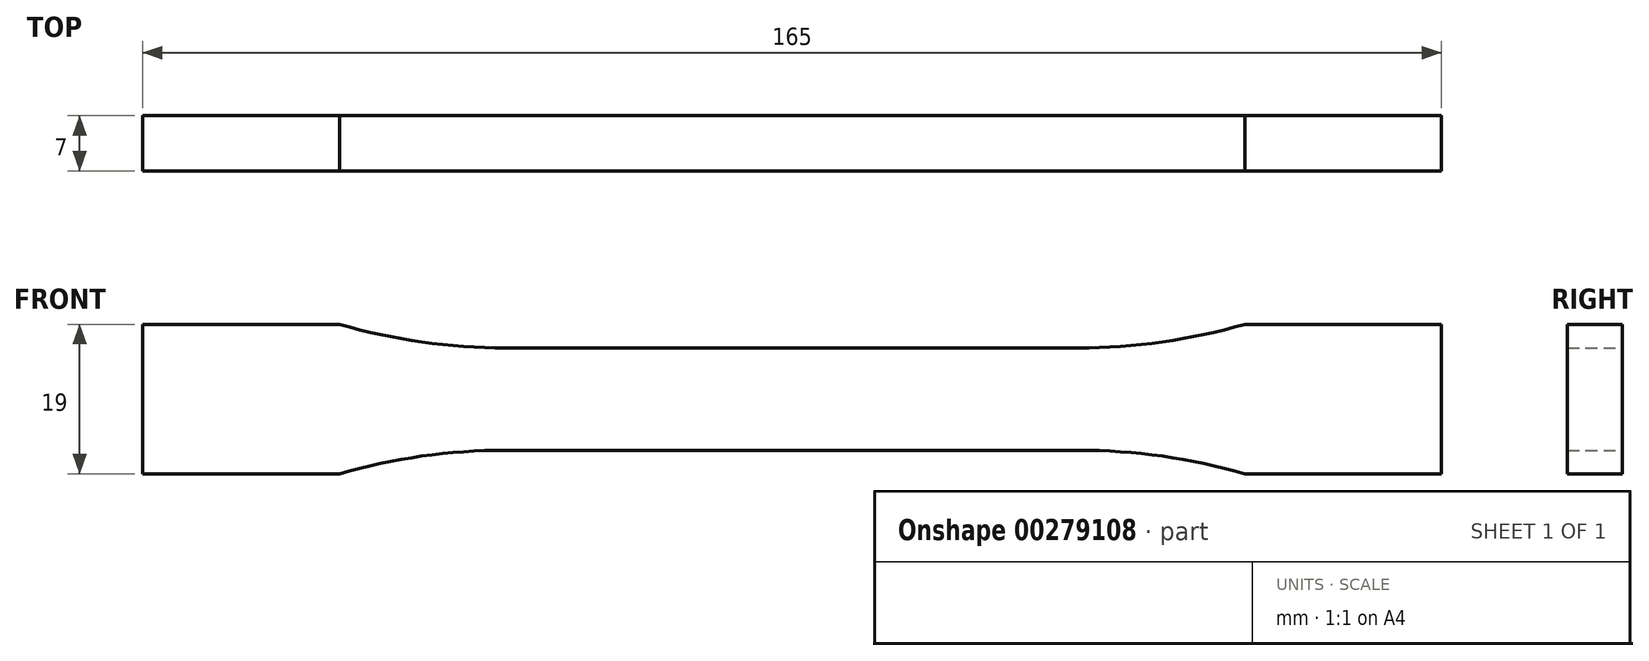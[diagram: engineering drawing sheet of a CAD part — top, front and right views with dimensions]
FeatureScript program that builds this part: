
annotation { "Feature Type Name" : "Feature", "Feature Type Description" : "" }
export const myFeature = defineFeature(function(context is Context, id is Id, definition is map)
    precondition{}
    {
        {
            var Q0;
            Q0=qCreatedBy(makeId("Front.planeOp"),FACE);
            var sketch = newSketch(context, id + "F0", { "sketchPlane" : qUnion([Q0])});
            skLineSegment(sketch, "E0", {"start": v(0, 6.5) * mm, "end": v(36.36, 6.5) * mm});
            skArc(sketch, "E1", {"start": v(36.36, 6.5) * mm, "mid": v(47.03, 7.25) * mm, "end": v(57.5, 9.5) * mm});
            skLineSegment(sketch, "E2", {"start": v(57.5, 9.5) * mm, "end": v(82.5, 9.5) * mm});
            skLineSegment(sketch, "E3.MirrorCS", {"start": v(57.5, -9.5) * mm, "end": v(82.5, -9.5) * mm});
            skLineSegment(sketch, "E4.MirrorCS", {"start": v(0, -6.5) * mm, "end": v(36.36, -6.5) * mm});
            skArc(sketch, "E5.MirrorCS", {"start": v(36.36, -6.5) * mm, "mid": v(47.03, -7.25) * mm, "end": v(57.5, -9.5) * mm});
            skArc(sketch, "E6.MirrorCS", {"start": v(-36.36, -6.5) * mm, "mid": v(-47.03, -7.25) * mm, "end": v(-57.5, -9.5) * mm});
            skLineSegment(sketch, "E7.MirrorCS", {"start": v(0, 6.5) * mm, "end": v(-36.36, 6.5) * mm});
            skArc(sketch, "E8.MirrorCS", {"start": v(-36.36, 6.5) * mm, "mid": v(-47.03, 7.25) * mm, "end": v(-57.5, 9.5) * mm});
            skLineSegment(sketch, "E9.MirrorCS", {"start": v(-57.5, -9.5) * mm, "end": v(-82.5, -9.5) * mm});
            skLineSegment(sketch, "E10.MirrorCS", {"start": v(0, -6.5) * mm, "end": v(-36.36, -6.5) * mm});
            skLineSegment(sketch, "E11.MirrorCS", {"start": v(-57.5, 9.5) * mm, "end": v(-82.5, 9.5) * mm});
            skLineSegment(sketch, "E12", {"start": v(-82.5, 9.5) * mm, "end": v(-82.5, -9.5) * mm});
            skLineSegment(sketch, "E13", {"start": v(82.5, 9.5) * mm, "end": v(82.5, -9.5) * mm});
            skSolve(sketch);
        }
        {
            var Q0;
            Q0=makeQuery(id+"F0.imprint","IMPRINT",FACE,{"disambiguationData":[TD([[makeQuery(id+"F0.imprint","IMPRINT",EDGE,{"derivedFrom":sQuery(id+"F0.wireOp",EDGE,"E0")}),-1.0]])]});
            extrude(context, id + "F1", {"entities" : qUnion([Q0]), "endBound" : BoundingType.SYMMETRIC, "depth" : 7 * mm});
        }
    });
